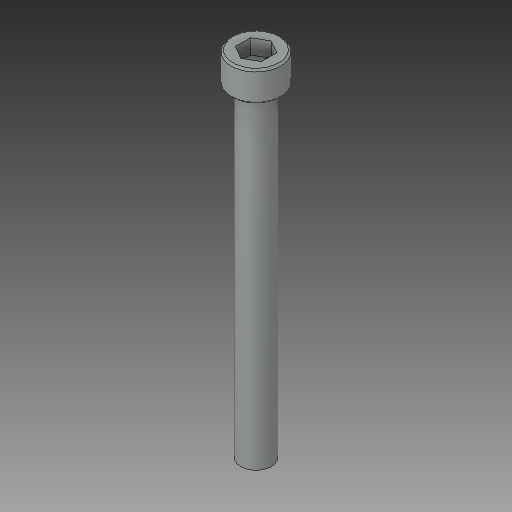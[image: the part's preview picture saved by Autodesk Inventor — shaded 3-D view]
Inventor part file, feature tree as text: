
AUTODESK INVENTOR PART (.ipt)
format: ipt  version: 2017 (Build 210142000, 142)  size: 94,720 bytes
history: native  units: in
note: dims shown in document units (in); Inventor stores cm internally (conversion verified against a paired STEP export)
features: chamfer x1
ambient origin geometry x8: Origin, YZ Plane, XZ Plane, XY Plane, X Axis, Y Axis, Z Axis, Center Point
bodies: Solid1 (feature_tree)
feature tree (1):
  chamfer  "Chamfer2"  [1 undecoded]
note: 1 required parameter value undecoded (feature->parameter linkage not recoverable at this tier; creation-order binding heuristic only, values carry confidence <= 0.55)
